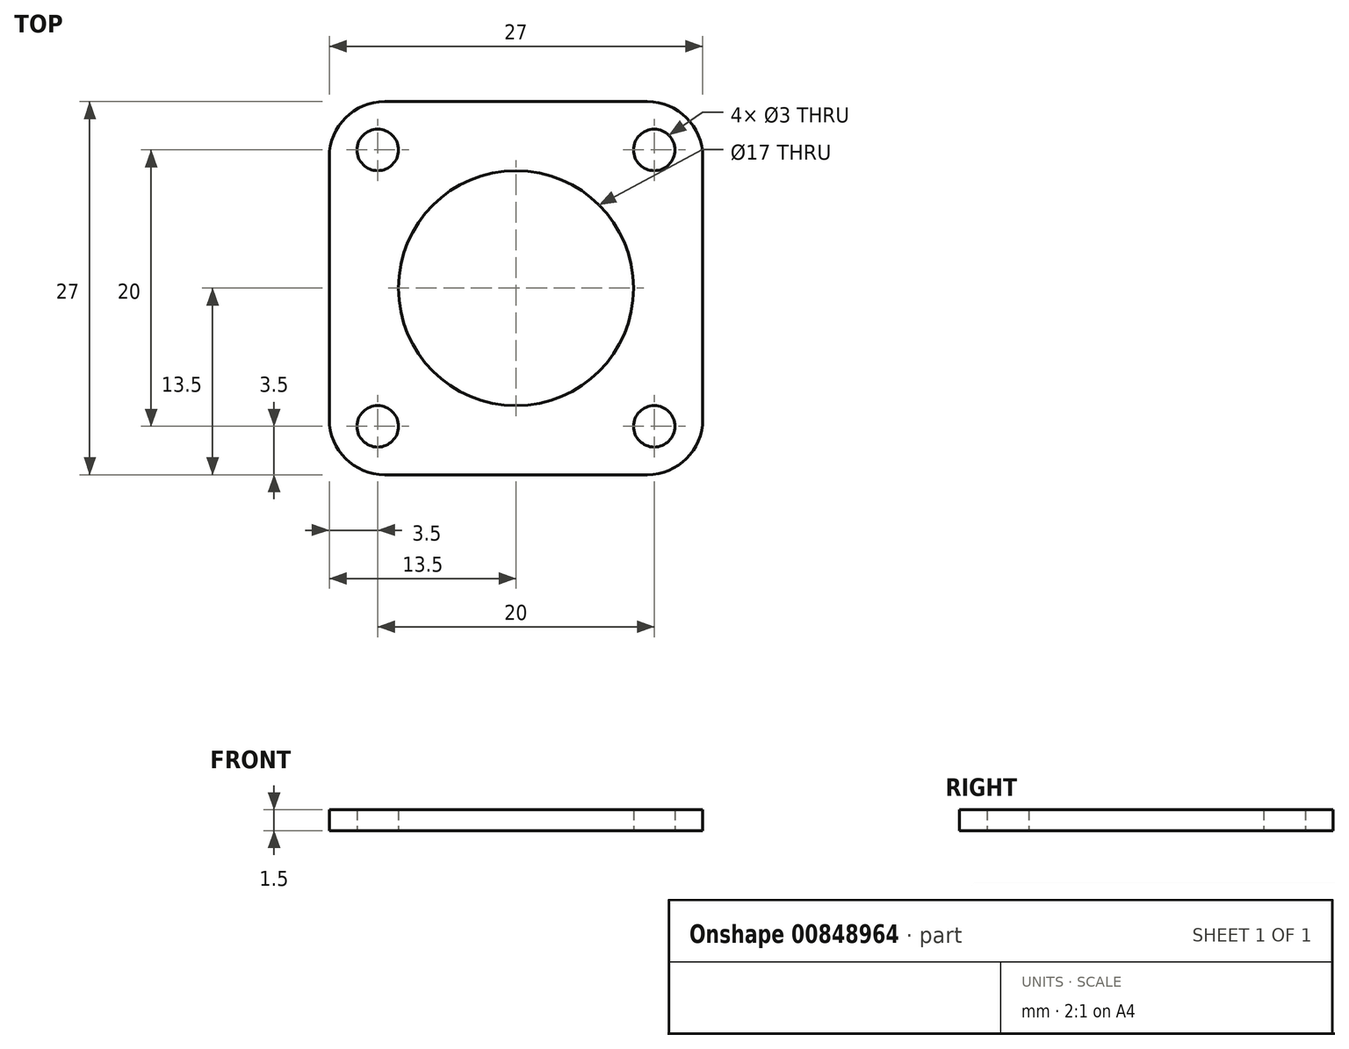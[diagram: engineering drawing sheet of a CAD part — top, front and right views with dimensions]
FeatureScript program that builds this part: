
annotation { "Feature Type Name" : "Feature", "Feature Type Description" : "" }
export const myFeature = defineFeature(function(context is Context, id is Id, definition is map)
    precondition{}
    {
        {
            var Q0;
            Q0=qCreatedBy(makeId("Top.planeOp"),FACE);
            var sketch = newSketch(context, id + "F0", { "sketchPlane" : qUnion([Q0])});
            skLineSegment(sketch, "E0.bottom", {"start": v(9.5, 13.5) * mm, "end": v(-9.5, 13.5) * mm});
            skLineSegment(sketch, "E0.top", {"start": v(9.5, -13.5) * mm, "end": v(-9.5, -13.5) * mm});
            skLineSegment(sketch, "E0.left", {"start": v(13.5, 9.5) * mm, "end": v(13.5, -9.5) * mm});
            skLineSegment(sketch, "E0.right", {"start": v(-13.5, 9.5) * mm, "end": v(-13.5, -9.5) * mm});
            skPoint(sketch, "E0.middle", {"position": v(0, 0) * mm});
            skCircle(sketch, "E1", {"center": v(-10, 10) * mm, "radius": 1.5 * mm});
            skCircle(sketch, "E2", {"center": v(0, 0) * mm, "radius": 8.5 * mm});
            skCircle(sketch, "E3.1.0", {"center": v(10, 10) * mm, "radius": 1.5 * mm});
            skCircle(sketch, "E3.2.0", {"center": v(10, -10) * mm, "radius": 1.5 * mm});
            skCircle(sketch, "E3.3.0", {"center": v(-10, -10) * mm, "radius": 1.5 * mm});
            skPoint(sketch, "E4.visualSharp", {"position": v(-13.5, 13.5) * mm});
            skArc(sketch, "E4.filletArc", {"start": v(-9.5, 13.5) * mm, "mid": v(-12.33, 12.33) * mm, "end": v(-13.5, 9.5) * mm});
            skPoint(sketch, "E5.visualSharp", {"position": v(13.5, 13.5) * mm});
            skArc(sketch, "E5.filletArc", {"start": v(13.5, 9.5) * mm, "mid": v(12.33, 12.33) * mm, "end": v(9.5, 13.5) * mm});
            skPoint(sketch, "E6.visualSharp", {"position": v(13.5, -13.5) * mm});
            skArc(sketch, "E6.filletArc", {"start": v(9.5, -13.5) * mm, "mid": v(12.33, -12.33) * mm, "end": v(13.5, -9.5) * mm});
            skPoint(sketch, "E7.visualSharp", {"position": v(-13.5, -13.5) * mm});
            skArc(sketch, "E7.filletArc", {"start": v(-13.5, -9.5) * mm, "mid": v(-12.33, -12.33) * mm, "end": v(-9.5, -13.5) * mm});
            skSolve(sketch);
        }
        {
            var Q0;
            Q0=makeQuery(id+"F0.imprint","IMPRINT",FACE,{"disambiguationData":[TD([[makeQuery(id+"F0.imprint","IMPRINT",EDGE,{"derivedFrom":sQuery(id+"F0.wireOp",EDGE,"E0.bottom")}),1.0]])]});
            extrude(context, id + "F1", {"entities" : qUnion([Q0]), "depth" : 1.5 * mm, "offsetDistance" : 25 * mm});
        }
    });
